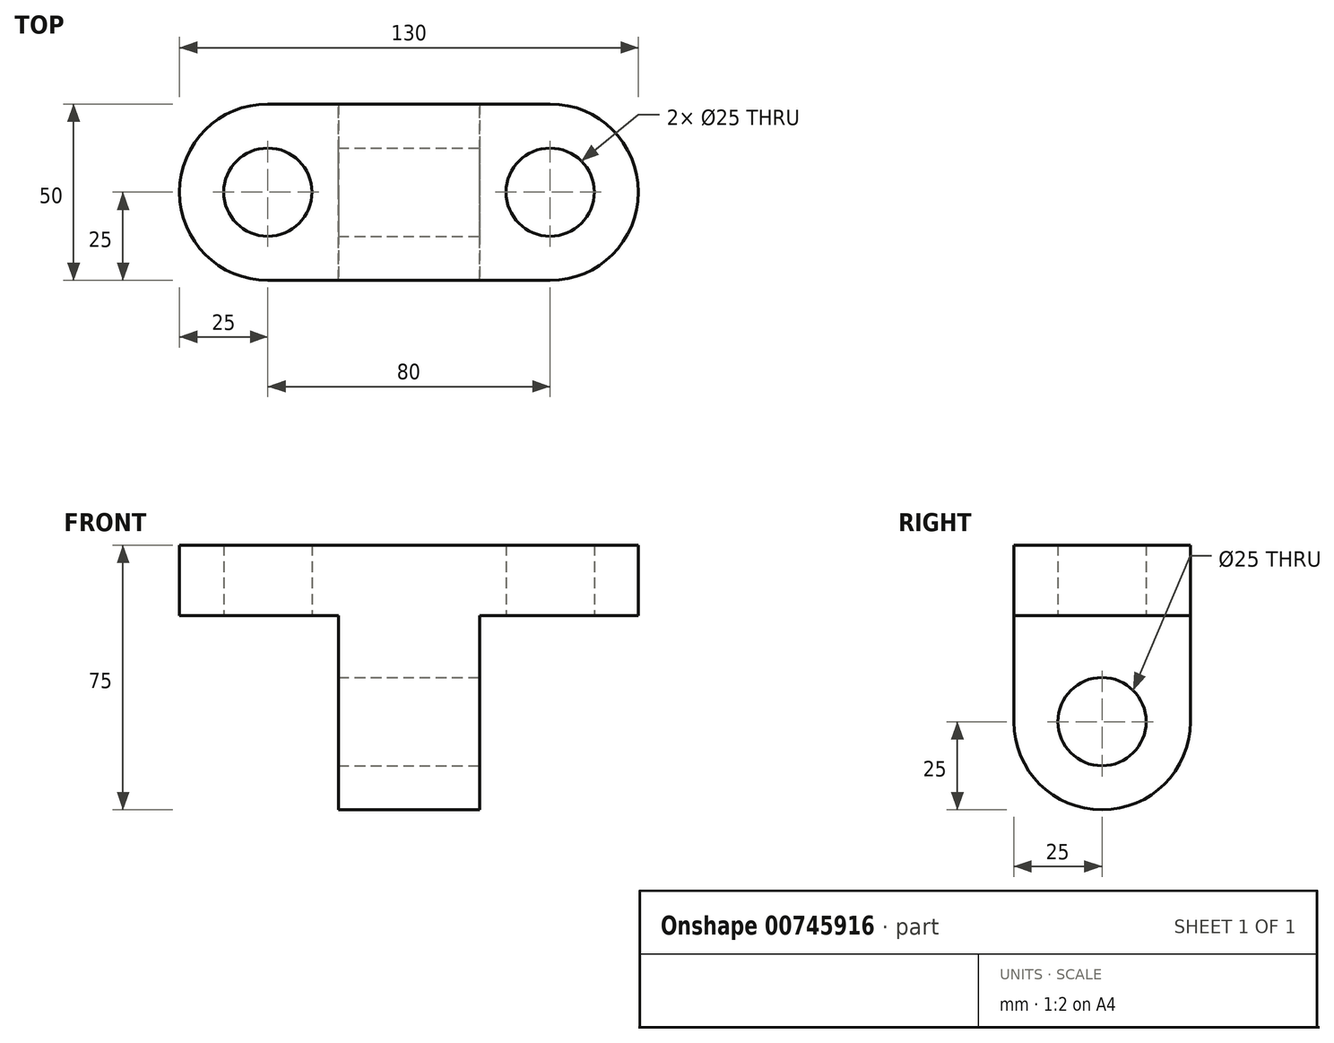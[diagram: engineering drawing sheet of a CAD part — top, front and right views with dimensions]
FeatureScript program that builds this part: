
annotation { "Feature Type Name" : "Feature", "Feature Type Description" : "" }
export const myFeature = defineFeature(function(context is Context, id is Id, definition is map)
    precondition{}
    {
        {
            var Q0;
            Q0=qCreatedBy(makeId("Top.planeOp"),FACE);
            var sketch = newSketch(context, id + "F0", { "sketchPlane" : qUnion([Q0])});
            skLineSegment(sketch, "E0.bottom", {"start": v(0, 0) * mm, "end": v(80, 0) * mm});
            skLineSegment(sketch, "E0.top", {"start": v(0, 50) * mm, "end": v(80, 50) * mm});
            skArc(sketch, "E1", {"start": v(80, 0) * mm, "mid": v(105, 25) * mm, "end": v(80, 50) * mm});
            skArc(sketch, "E2", {"start": v(0, 50) * mm, "mid": v(-25, 25) * mm, "end": v(0, 0) * mm});
            skLineSegment(sketch, "E3.bottom", {"start": v(20, 50) * mm, "end": v(60, 50) * mm});
            skLineSegment(sketch, "E3.top", {"start": v(20, 0) * mm, "end": v(60, 0) * mm});
            skLineSegment(sketch, "E3.left", {"start": v(20, 50) * mm, "end": v(20, 0) * mm});
            skLineSegment(sketch, "E3.right", {"start": v(60, 50) * mm, "end": v(60, 0) * mm});
            skCircle(sketch, "E4", {"center": v(80, 25) * mm, "radius": 12.5 * mm});
            skCircle(sketch, "E5", {"center": v(0, 25) * mm, "radius": 12.5 * mm});
            skLineSegment(sketch, "E6", {"start": v(80, 25) * mm, "end": v(60, 25) * mm, "construction": true});
            skLineSegment(sketch, "E7", {"start": v(0, 25) * mm, "end": v(20, 25) * mm, "construction": true});
            skSolve(sketch);
        }
        {
            var Q0;
            {var subQ0=sQuery(id+"F0.wireOp",EDGE,"E3.left");var subQ8=makeQuery(id+"F0.imprint","IMPRINT",EDGE,{"derivedFrom":subQ0});var subQ10=sQuery(id+"F0.wireOp",EDGE,"E2");var subQ11=sQuery(id+"F0.wireOp",EDGE,"E1");Q0=qUnion([makeQuery(id+"F0.imprint","IMPRINT",FACE,{"disambiguationData":[TD([[makeQuery(id+"F0.imprint","IMPRINT",EDGE,{"derivedFrom":subQ11}),1.0]])]}),makeQuery(id+"F0.imprint","IMPRINT",FACE,{"disambiguationData":[TD([[makeQuery(id+"F0.imprint","IMPRINT",EDGE,{"derivedFrom":subQ10}),1.0]])]}),makeQuery(id+"F0.imprint","IMPRINT",FACE,{"disambiguationData":[TD([[subQ8,1.0]])]})]);}
            extrude(context, id + "F1", {"entities" : qUnion([Q0]), "depth" : 20 * mm, "offsetDistance" : 25 * mm});
        }
        {
            var Q0;
            {var subQ0=sQuery(id+"F0.wireOp",EDGE,"E3.left");Q0=makeQuery(id+"F0.imprint","IMPRINT",FACE,{"disambiguationData":[TD([[makeQuery(id+"F0.imprint","IMPRINT",EDGE,{"derivedFrom":subQ0}),1.0]])]});}
            extrude(context, id + "F2", {"entities" : qUnion([Q0]), "operationType" : NewBodyOperationType.ADD, "oppositeDirection" : true, "depth" : 30 * mm, "offsetDistance" : 25 * mm});
        }
        {
            var Q0;
            Q0=makeQuery(id+"F2.opExtrude","SWEPT_FACE",FACE,{"disambiguationData":[OSD([sQuery(id+"F0.wireOp",EDGE,"E3.right")])]});
            var sketch = newSketch(context, id + "F3", { "sketchPlane" : qUnion([Q0])});
            skArc(sketch, "E8", {"start": v(0, -30) * mm, "mid": v(25, -55) * mm, "end": v(50, -30) * mm});
            skCircle(sketch, "E9", {"center": v(25, -30) * mm, "radius": 12.5 * mm});
            skSolve(sketch);
        }
        {
            var Q0;
            Q0 = qSketchRegion(id + "F3", true);
            var Q1;
            Q1=makeQuery(id+"F3.imprint","IMPRINT",FACE,{"disambiguationData":[TD([[makeQuery(id+"F3.imprint","IMPRINT",EDGE,{"derivedFrom":sQuery(id+"F3.wireOp",EDGE,"E8")}),1.0]])]});
            extrude(context, id + "F4", {"entities" : qUnion([Q0, Q1]), "operationType" : NewBodyOperationType.ADD, "oppositeDirection" : true, "depth" : 40 * mm, "offsetDistance" : 25 * mm});
        }
        {
            var Q0;
            Q0 = qSketchRegion(id + "F3", true);
            extrude(context, id + "F5", {"entities" : qUnion([Q0]), "operationType" : NewBodyOperationType.REMOVE, "endBound" : BoundingType.THROUGH_ALL, "oppositeDirection" : true, "depth" : 25 * mm, "offsetDistance" : 25 * mm});
        }
    });
